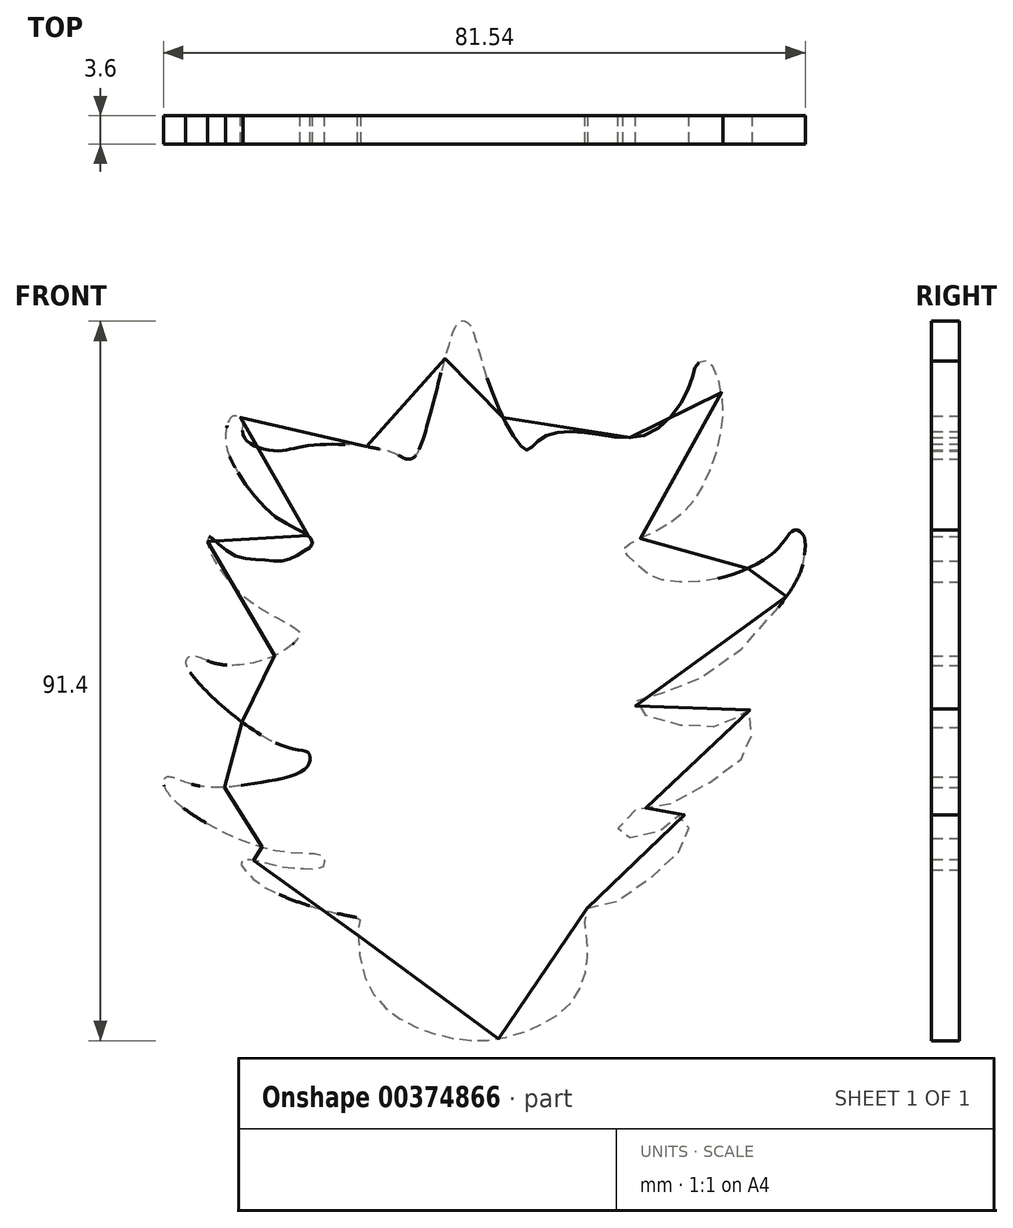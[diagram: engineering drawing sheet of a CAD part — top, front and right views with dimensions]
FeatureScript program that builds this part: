
annotation { "Feature Type Name" : "Feature", "Feature Type Description" : "" }
export const myFeature = defineFeature(function(context is Context, id is Id, definition is map)
    precondition{}
    {
        {
            var Q0;
            Q0=qCreatedBy(makeId("Front.planeOp"),FACE);
            var sketch = newSketch(context, id + "F0", { "sketchPlane" : qUnion([Q0])});
            skFitSpline(sketch, "E0", {"points": [v(-34.55, -15.96) * mm, v(-32.03, -15.52) * mm, v(-27.88, -13.12) * mm, v(-23.84, -9.9) * mm, v(-22.4, -7.96) * mm, v(-21.64, -5.81) * mm, v(-22.02, -4.24) * mm, v(-22.77, -4.18) * mm, v(-23.84, -4.93) * mm, v(-25.54, -6.32) * mm, v(-28.7, -6.95) * mm, v(-29.83, -7.07) * mm, v(-30.52, -6.32) * mm, v(-30.52, -5.44) * mm, v(-28.76, -3.55) * mm, v(-25.48, -3.1) * mm, v(-20.38, -0.84) * mm, v(-15.86, 2.21) * mm, v(-13.97, 4.35) * mm, v(-13.66, 6.37) * mm, v(-13.72, 9.08) * mm, v(-14.22, 9.27) * mm, v(-15.23, 9.2) * mm, v(-15.92, 7.88) * mm, v(-17.56, 7.25) * mm, v(-19.45, 7) * mm, v(-23.67, 7.44) * mm, v(-27.2, 8.58) * mm, v(-28.4, 9.65) * mm, v(-28.21, 10.4) * mm, v(-26.13, 11.1) * mm, v(-23.17, 12.04) * mm, v(-17.81, 14.62) * mm, v(-11.2, 21.05) * mm, v(-7.48, 26.72) * mm, v(-6.91, 29.37) * mm, v(-6.98, 31.2) * mm, v(-7.73, 32.02) * mm, v(-8.49, 31.95) * mm, v(-9.25, 31.07) * mm, v(-11.14, 29) * mm, v(-16.55, 26.28) * mm, v(-22.54, 25.46) * mm, v(-26.64, 26.34) * mm, v(-28.84, 28.3) * mm, v(-29.98, 29.43) * mm, v(-29.47, 30.19) * mm, v(-27.14, 31.32) * mm, v(-23.3, 33.53) * mm, v(-20.84, 36.05) * mm, v(-18.7, 40.33) * mm, v(-17.37, 45.81) * mm, v(-17.69, 50.48) * mm, v(-19.01, 53.38) * mm, v(-19.77, 53.5) * mm, v(-20.52, 53.25) * mm, v(-21.03, 52.05) * mm, v(-22.48, 48.46) * mm, v(-26.76, 44.3) * mm, v(-31.61, 43.99) * mm, v(-36.34, 44.55) * mm, v(-39.62, 44.11) * mm, v(-41.25, 42.98) * mm, v(-42.14, 42.22) * mm, v(-42.83, 42.6) * mm, v(-45.16, 46.2) * mm, v(-47.24, 51.36) * mm, v(-48.5, 55.64) * mm, v(-49.5, 58.23) * mm, v(-50.4, 58.6) * mm, v(-51.2, 58.04) * mm, v(-51.97, 56.21) * mm, v(-53.23, 51.67) * mm, v(-54.86, 45.44) * mm, v(-56.12, 41.9) * mm, v(-56.82, 41.15) * mm, v(-57.7, 41.15) * mm, v(-58.83, 41.72) * mm, v(-61.8, 42.54) * mm, v(-66.58, 42.98) * mm, v(-71.18, 42.6) * mm, v(-73.33, 42.16) * mm, v(-76.41, 42.6) * mm, v(-78.24, 44.11) * mm, v(-78.3, 45.94) * mm, v(-78.8, 46.5) * mm, v(-79.63, 46.5) * mm, v(-80.13, 45.81) * mm, v(-80.5, 43.67) * mm, v(-79.31, 40.08) * mm, v(-74.08, 33.72) * mm, v(-70.11, 31.45) * mm, v(-69.48, 30.31) * mm, v(-70.55, 29.37) * mm, v(-72.95, 28.23) * mm, v(-75.72, 28.3) * mm, v(-79.63, 29) * mm, v(-82.27, 31.13) * mm, v(-82.65, 31.2) * mm, v(-82.65, 29.87) * mm, v(-79.94, 25.46) * mm, v(-75.34, 21.68) * mm, v(-71.18, 19.22) * mm, v(-71.12, 18.66) * mm, v(-72.25, 17.33) * mm, v(-76.54, 15.32) * mm, v(-81.96, 15.2) * mm, v(-84.8, 16.07) * mm, v(-85.55, 15.32) * mm, v(-83.97, 12.73) * mm, v(-78.68, 7.88) * mm, v(-72.32, 4.35) * mm, v(-70.05, 3.85) * mm, v(-69.73, 3.03) * mm, v(-70.55, 1.58) * mm, v(-76.1, 0) * mm, v(-81.52, -0.62) * mm, v(-85.49, 0) * mm, v(-87.94, 0.7) * mm, v(-88.38, 0) * mm, v(-86.5, -2.7) * mm, v(-77.99, -7.5) * mm, v(-71.5, -8.94) * mm, v(-68.54, -9.13) * mm, v(-67.97, -9.76) * mm, v(-68.22, -10.83) * mm, v(-70.93, -10.96) * mm, v(-73.64, -10.7) * mm, v(-76.85, -9.89) * mm, v(-78.56, -10.01) * mm, v(-78.11, -11.02) * mm, v(-75.66, -13.22) * mm, v(-66.58, -16.56) * mm, v(-63.3, -17.32) * mm, v(-63.5, -17.57) * mm, v(-63.12, -23.62) * mm, v(-60.35, -28.47) * mm, v(-56, -31.18) * mm, v(-50.7, -32.63) * mm, v(-45.92, -32.57) * mm, v(-40.25, -30.68) * mm, v(-36.47, -27.78) * mm, v(-34.76, -24.06) * mm, v(-34.58, -20.03) * mm, v(-34.55, -15.96) * mm]});
            skSolve(sketch);
        }
        {
            var Q0;
            Q0 = qSketchRegion(id + "F0", true);
            extrude(context, id + "F1", {"entities" : qUnion([Q0]), "depth" : 3.6 * mm});
        }
    });
